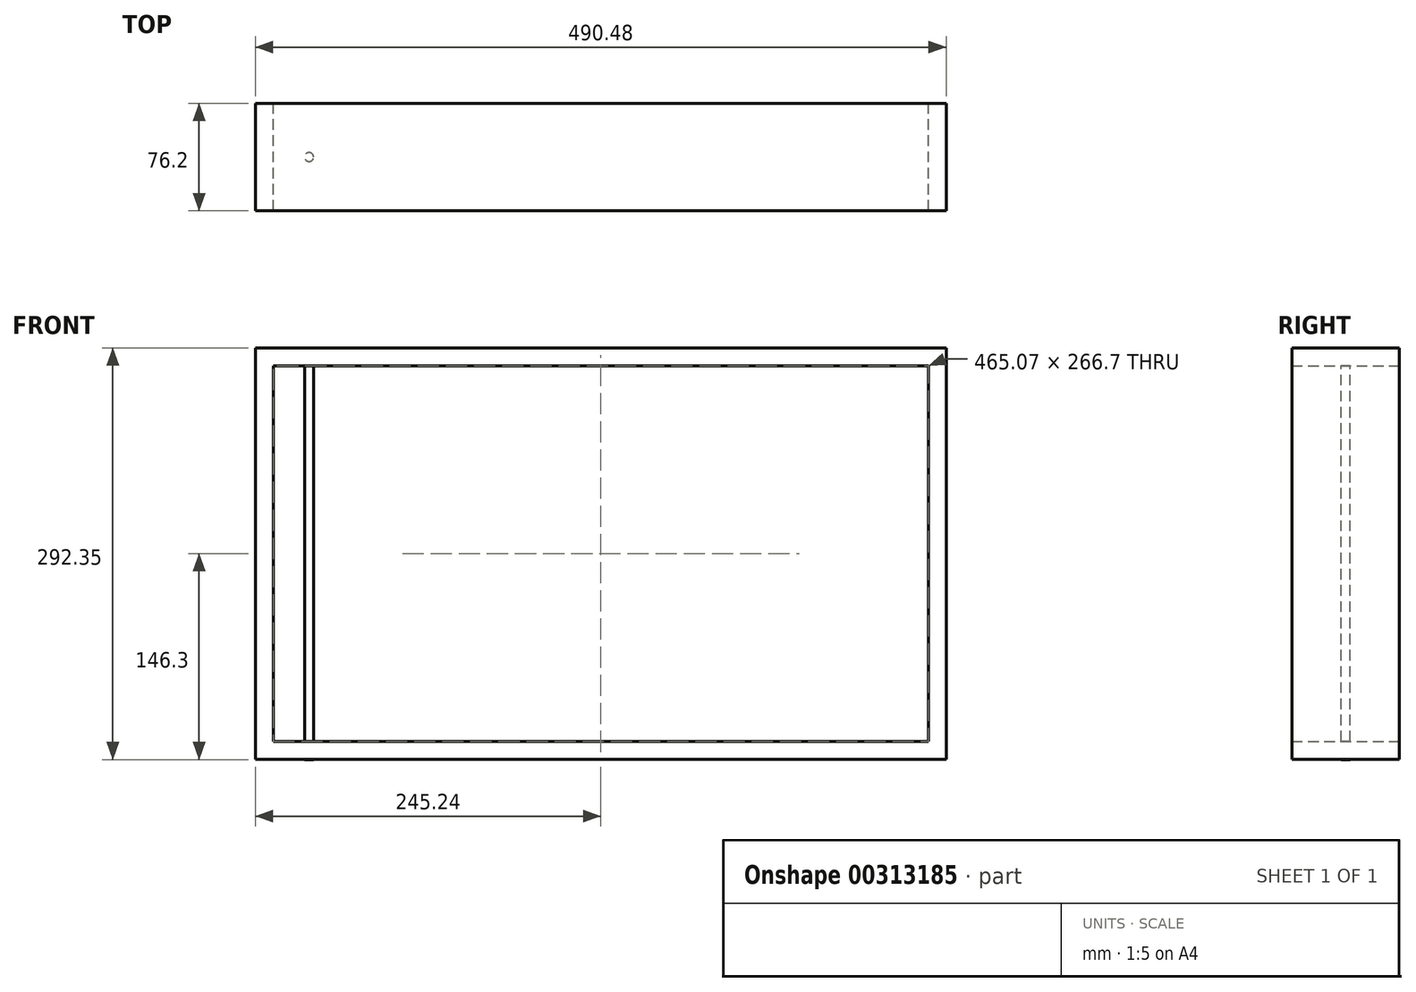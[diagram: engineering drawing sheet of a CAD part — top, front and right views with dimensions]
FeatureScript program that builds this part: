
annotation { "Feature Type Name" : "Feature", "Feature Type Description" : "" }
export const myFeature = defineFeature(function(context is Context, id is Id, definition is map)
    precondition{}
    {
        {
            var Q0;
            Q0=qCreatedBy(makeId("Front.planeOp"),FACE);
            var sketch = newSketch(context, id + "F0", { "sketchPlane" : qUnion([Q0])});
            skLineSegment(sketch, "E0.bottom", {"start": v(-245.24, -146.05) * mm, "end": v(245.24, -146.05) * mm});
            skLineSegment(sketch, "E0.top", {"start": v(-245.24, 146.05) * mm, "end": v(245.24, 146.05) * mm});
            skLineSegment(sketch, "E0.left", {"start": v(-245.24, -146.05) * mm, "end": v(-245.24, 146.05) * mm});
            skLineSegment(sketch, "E0.right", {"start": v(245.24, -146.05) * mm, "end": v(245.24, 146.05) * mm});
            skPoint(sketch, "E0.middle", {"position": v(0, 0) * mm});
            skLineSegment(sketch, "E1.bottom", {"start": v(-232.54, -133.35) * mm, "end": v(232.54, -133.35) * mm});
            skLineSegment(sketch, "E1.top", {"start": v(-232.54, 133.35) * mm, "end": v(232.54, 133.35) * mm});
            skLineSegment(sketch, "E1.left", {"start": v(-232.54, -133.35) * mm, "end": v(-232.54, 133.35) * mm});
            skLineSegment(sketch, "E1.right", {"start": v(232.54, -133.35) * mm, "end": v(232.54, 133.35) * mm});
            skSolve(sketch);
        }
        {
            var Q0;
            Q0 = qSketchRegion(id + "F0", true);
            extrude(context, id + "F1", {"entities" : qUnion([Q0]), "endBound" : BoundingType.SYMMETRIC, "depth" : 76.2 * mm});
        }
        {
            var Q0;
            Q0=makeQuery(id+"F1.opExtrude","SWEPT_FACE",FACE,{"disambiguationData":[OSD([sQuery(id+"F0.wireOp",EDGE,"E0.top")])]});
            var sketch = newSketch(context, id + "F2", { "sketchPlane" : qUnion([Q0])});
            skLineSegment(sketch, "E2", {"start": v(-245.24, 0) * mm, "end": v(-207.14, 0) * mm, "construction": true});
            skPoint(sketch, "E2.endSnap0", {"position": v(-245.24, 0) * mm});
            skCircle(sketch, "E3", {"center": v(-207.14, 0) * mm, "radius": 3.18 * mm});
            skSolve(sketch);
        }
        {
            var Q0;
            Q0=makeQuery(id+"F2.imprint","IMPRINT",FACE,{"disambiguationData":[TD([[makeQuery(id+"F2.imprint","IMPRINT",EDGE,{"derivedFrom":sQuery(id+"F2.wireOp",EDGE,"E3")}),1.0]])]});
            extrude(context, id + "F3", {"entities" : qUnion([Q0]), "operationType" : NewBodyOperationType.ADD, "oppositeDirection" : true, "depth" : 292.35 * mm});
        }
    });
